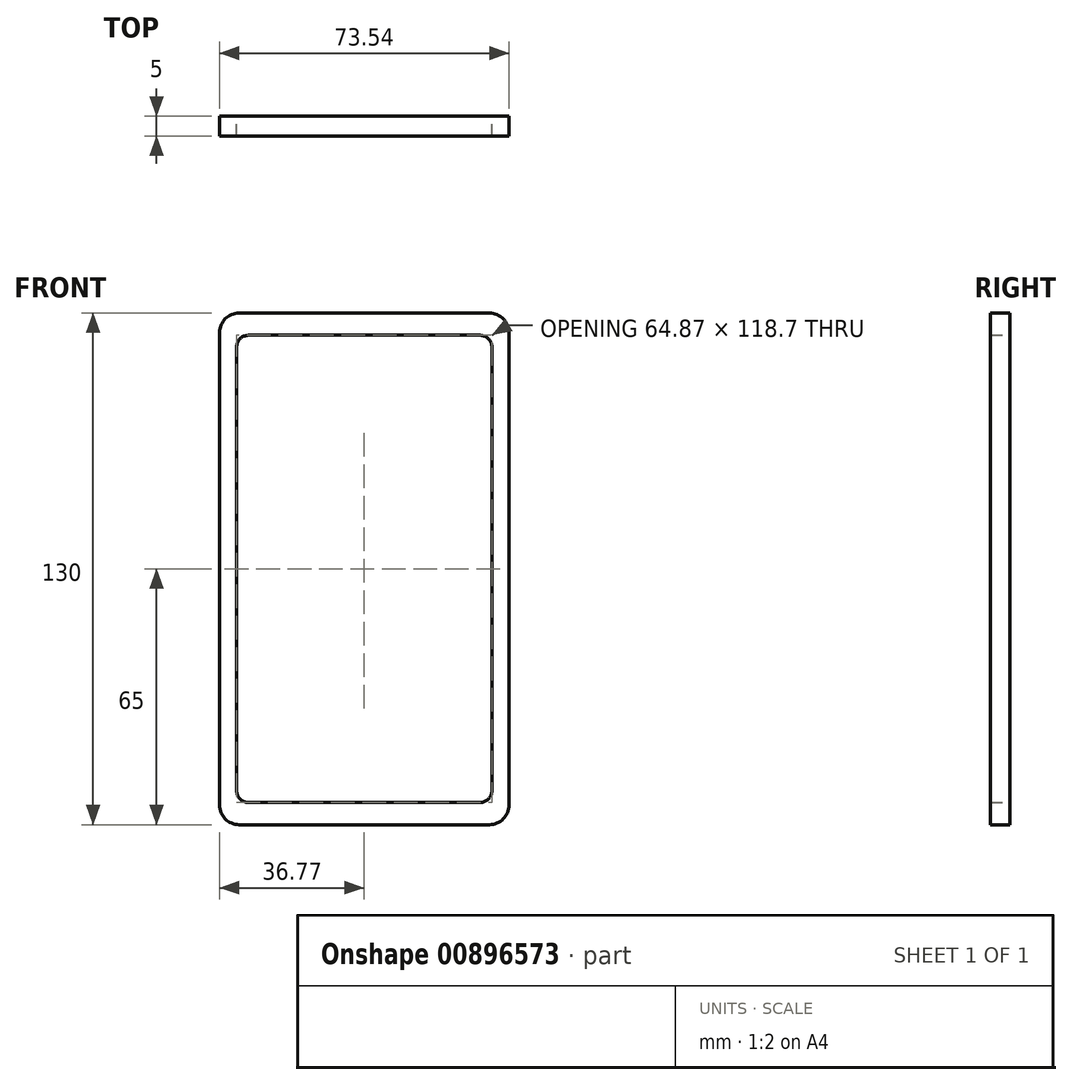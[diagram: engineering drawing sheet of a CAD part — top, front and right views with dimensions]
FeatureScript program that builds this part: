
annotation { "Feature Type Name" : "Feature", "Feature Type Description" : "" }
export const myFeature = defineFeature(function(context is Context, id is Id, definition is map)
    precondition{}
    {
        {
            var Q0;
            Q0=qCreatedBy(makeId("Front.planeOp"),FACE);
            var sketch = newSketch(context, id + "F0", { "sketchPlane" : qUnion([Q0])});
            skLineSegment(sketch, "E0.bottom", {"start": v(-36.77, -65) * mm, "end": v(36.77, -65) * mm});
            skLineSegment(sketch, "E0.top", {"start": v(-36.77, 65) * mm, "end": v(36.77, 65) * mm});
            skLineSegment(sketch, "E0.left", {"start": v(-36.77, -65) * mm, "end": v(-36.77, 65) * mm});
            skLineSegment(sketch, "E0.right", {"start": v(36.77, -65) * mm, "end": v(36.77, 65) * mm});
            skPoint(sketch, "E0.middle", {"position": v(0, 0) * mm});
            skLineSegment(sketch, "E1.bottom", {"start": v(32.44, -59.35) * mm, "end": v(-32.44, -59.35) * mm});
            skLineSegment(sketch, "E1.top", {"start": v(32.44, 59.35) * mm, "end": v(-32.43, 59.35) * mm});
            skLineSegment(sketch, "E1.left", {"start": v(32.44, -59.35) * mm, "end": v(32.44, 59.35) * mm});
            skLineSegment(sketch, "E1.right", {"start": v(-32.44, -59.35) * mm, "end": v(-32.43, 59.35) * mm});
            skSolve(sketch);
        }
        {
            var Q0;
            Q0=makeQuery(id+"F0.imprint","IMPRINT",FACE,{"disambiguationData":[TD([[makeQuery(id+"F0.imprint","IMPRINT",EDGE,{"derivedFrom":sQuery(id+"F0.wireOp",EDGE,"E0.bottom")}),1.0]])]});
            extrude(context, id + "F1", {"entities" : qUnion([Q0]), "depth" : 5 * mm, "offsetDistance" : 25 * mm});
        }
        {
            var Q0;
            Q0=makeQuery(id+"F1.opExtrude","SWEPT_EDGE",EDGE,{"disambiguationData":[OSD([sQuery(id+"F0.wireOp",EDGE,"E0.top"),sQuery(id+"F0.wireOp",EDGE,"E0.left")])]});
            var Q1;
            Q1=makeQuery(id+"F1.opExtrude","SWEPT_EDGE",EDGE,{"disambiguationData":[OSD([sQuery(id+"F0.wireOp",EDGE,"E0.top"),sQuery(id+"F0.wireOp",EDGE,"E0.right")])]});
            var Q2;
            Q2=makeQuery(id+"F1.opExtrude","SWEPT_EDGE",EDGE,{"disambiguationData":[OSD([sQuery(id+"F0.wireOp",EDGE,"E0.bottom"),sQuery(id+"F0.wireOp",EDGE,"E0.right")])]});
            var Q3;
            Q3=makeQuery(id+"F1.opExtrude","SWEPT_EDGE",EDGE,{"disambiguationData":[OSD([sQuery(id+"F0.wireOp",EDGE,"E0.bottom"),sQuery(id+"F0.wireOp",EDGE,"E0.left")])]});
            fillet(context, id + "F2", {"entities" : qUnion([Q0, Q1, Q2, Q3]), "radius" : 5 * mm, "tangentPropagation" : true, "allowEdgeOverflow" : false});
        }
        {
            var Q0;
            Q0=makeQuery(id+"F1.opExtrude","SWEPT_EDGE",EDGE,{"disambiguationData":[OSD([sQuery(id+"F0.wireOp",EDGE,"E1.top"),sQuery(id+"F0.wireOp",EDGE,"E1.left")])]});
            var Q1;
            Q1=makeQuery(id+"F1.opExtrude","SWEPT_EDGE",EDGE,{"disambiguationData":[OSD([sQuery(id+"F0.wireOp",EDGE,"E1.bottom"),sQuery(id+"F0.wireOp",EDGE,"E1.left")])]});
            var Q2;
            Q2=makeQuery(id+"F1.opExtrude","SWEPT_EDGE",EDGE,{"disambiguationData":[OSD([sQuery(id+"F0.wireOp",EDGE,"E1.top"),sQuery(id+"F0.wireOp",EDGE,"E1.right")])]});
            var Q3;
            Q3=makeQuery(id+"F1.opExtrude","SWEPT_EDGE",EDGE,{"disambiguationData":[OSD([sQuery(id+"F0.wireOp",EDGE,"E1.bottom"),sQuery(id+"F0.wireOp",EDGE,"E1.right")])]});
            fillet(context, id + "F3", {"entities" : qUnion([Q0, Q1, Q2, Q3]), "radius" : 3 * mm, "tangentPropagation" : true, "allowEdgeOverflow" : false});
        }
    });
